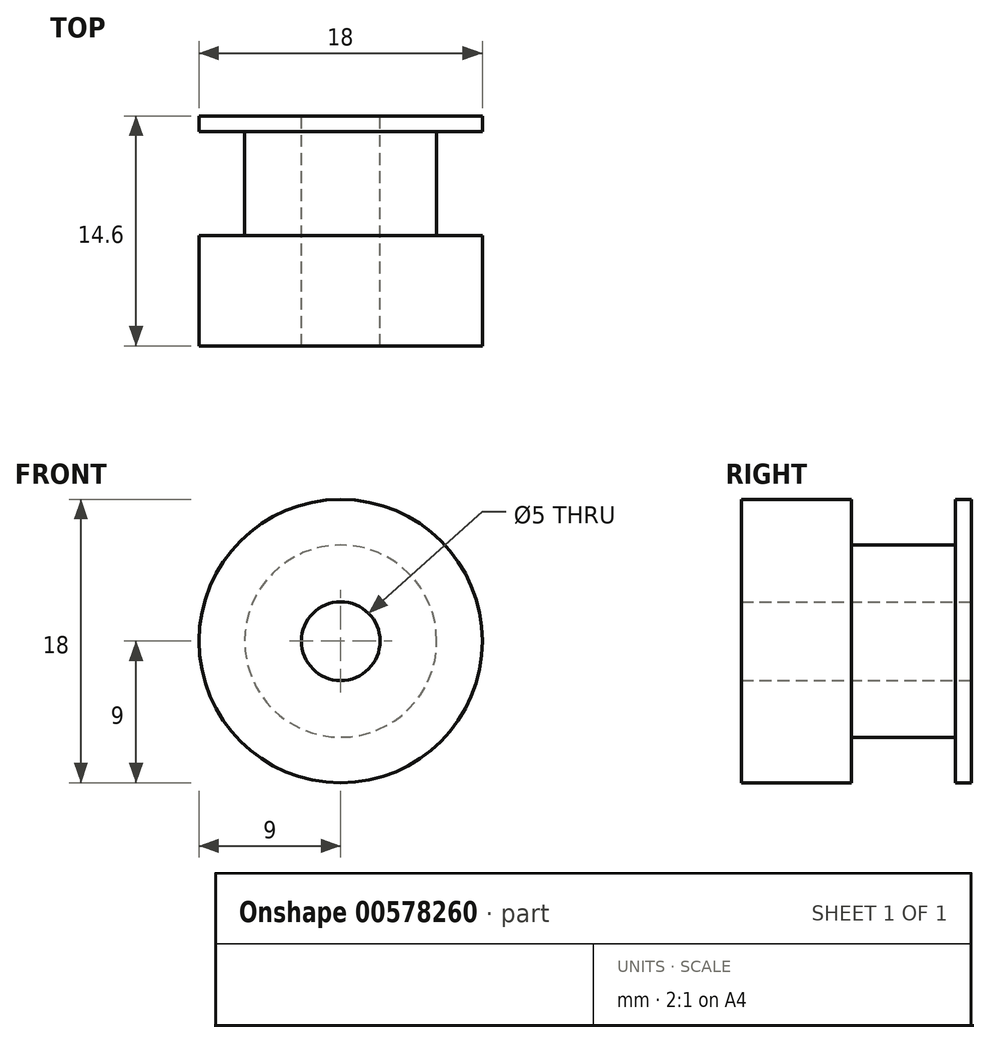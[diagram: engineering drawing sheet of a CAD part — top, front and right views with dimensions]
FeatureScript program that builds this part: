
annotation { "Feature Type Name" : "Feature", "Feature Type Description" : "" }
export const myFeature = defineFeature(function(context is Context, id is Id, definition is map)
    precondition{}
    {
        {
            var Q0;
            Q0=qCreatedBy(makeId("Front.planeOp"),FACE);
            var sketch = newSketch(context, id + "F0", { "sketchPlane" : qUnion([Q0])});
            skCircle(sketch, "E0", {"center": v(0, 0) * mm, "radius": 9 * mm});
            skCircle(sketch, "E1", {"center": v(0, 0) * mm, "radius": 2.5 * mm});
            skCircle(sketch, "E2", {"center": v(0, 0) * mm, "radius": 6.1 * mm});
            skSolve(sketch);
        }
        {
            var Q0;
            Q0 = qSketchRegion(id + "F0", true);
            var Q1;
            Q1=makeQuery(id+"F0.imprint","IMPRINT",FACE,{"disambiguationData":[TD([[makeQuery(id+"F0.imprint","IMPRINT",EDGE,{"derivedFrom":sQuery(id+"F0.wireOp",EDGE,"E1")}),-1.0]])]});
            extrude(context, id + "F1", {"entities" : qUnion([Q0, Q1]), "depth" : 14.6 * mm, "offsetDistance" : 25 * mm});
        }
        {
            var Q0;
            Q0=makeQuery(id+"F0.imprint","IMPRINT",FACE,{"disambiguationData":[TD([[makeQuery(id+"F0.imprint","IMPRINT",EDGE,{"derivedFrom":sQuery(id+"F0.wireOp",EDGE,"E0")}),1.0]])]});
            extrude(context, id + "F2", {"entities" : qUnion([Q0]), "operationType" : NewBodyOperationType.REMOVE, "depth" : 7.6 * mm, "offsetDistance" : 25 * mm, "hasSecondDirection" : true, "secondDirectionOppositeDirection" : false, "secondDirectionDepth" : 1 * mm});
        }
    });
